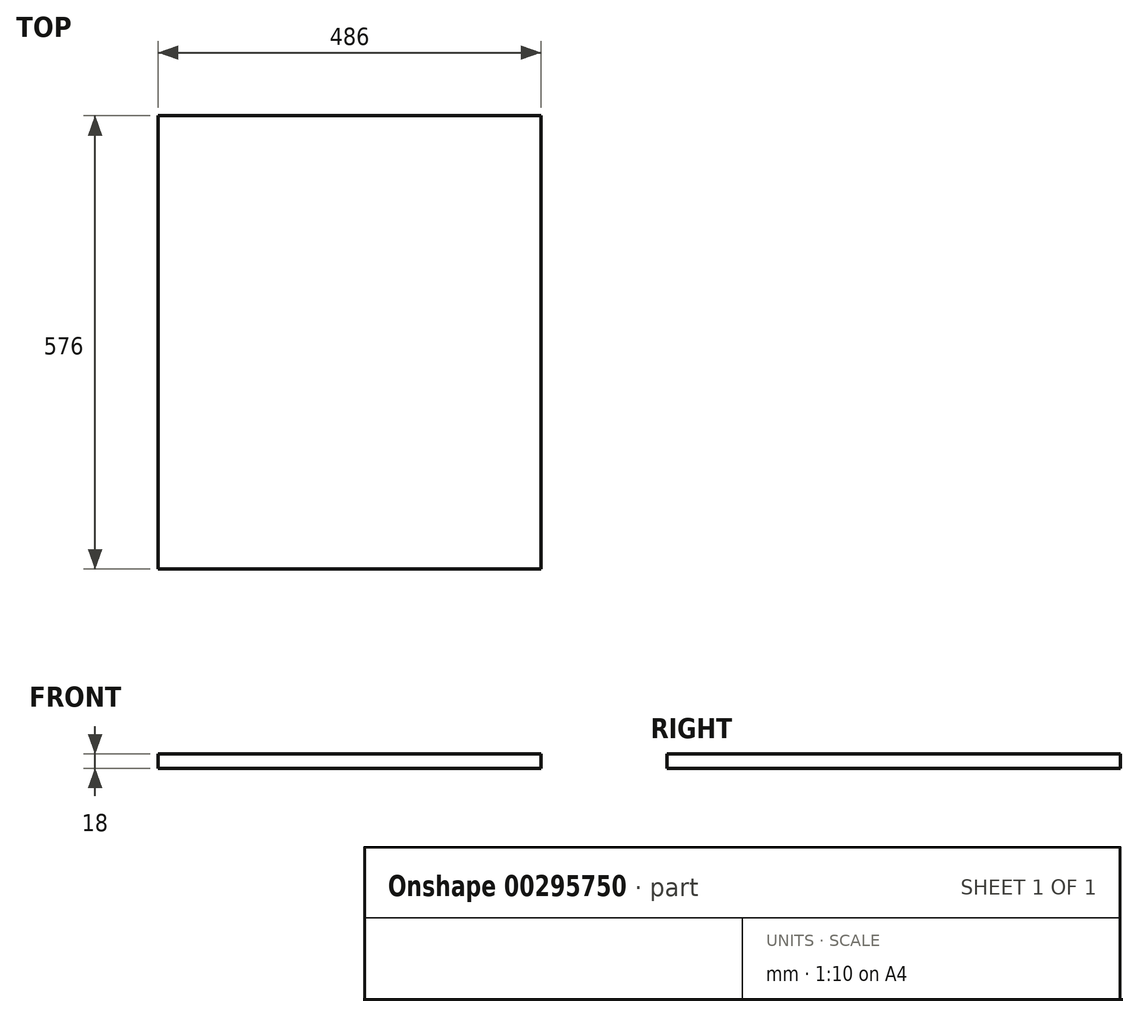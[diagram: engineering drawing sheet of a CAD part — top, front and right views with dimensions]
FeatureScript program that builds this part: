
annotation { "Feature Type Name" : "Feature", "Feature Type Description" : "" }
export const myFeature = defineFeature(function(context is Context, id is Id, definition is map)
    precondition{}
    {
        {
            var Q0;
            Q0=qCreatedBy(makeId("Top.planeOp"),FACE);
            var sketch = newSketch(context, id + "F0", { "sketchPlane" : qUnion([Q0])});
            skLineSegment(sketch, "E0.bottom", {"start": v(-229.88, 399.1) * mm, "end": v(256.12, 399.1) * mm});
            skLineSegment(sketch, "E0.top", {"start": v(-229.88, -176.9) * mm, "end": v(256.12, -176.9) * mm});
            skLineSegment(sketch, "E0.left", {"start": v(-229.88, 399.1) * mm, "end": v(-229.88, -176.9) * mm});
            skLineSegment(sketch, "E0.right", {"start": v(256.12, 399.1) * mm, "end": v(256.12, -176.9) * mm});
            skSolve(sketch);
        }
        {
            var Q0;
            Q0 = qSketchRegion(id + "F0", true);
            extrude(context, id + "F1", {"entities" : qUnion([Q0]), "depth" : 18 * mm});
        }
    });
